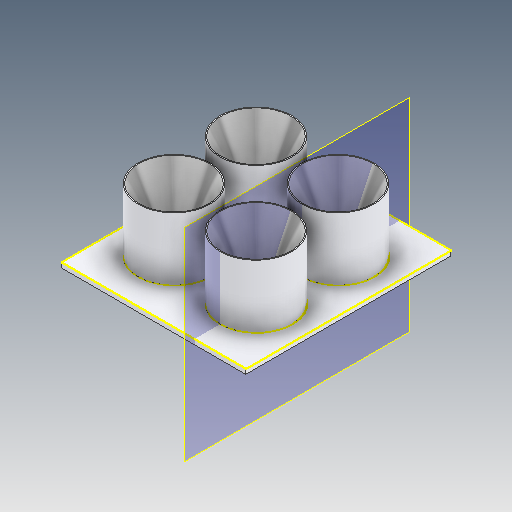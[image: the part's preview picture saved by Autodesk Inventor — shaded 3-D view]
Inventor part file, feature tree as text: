
AUTODESK INVENTOR PART (.ipt)
format: ipt  version: 2020.3 (Build 243373010, 373A)  size: 189,952 bytes
history: native  units: mm
features: other x3, sketch x2, plane x1
ambient origin geometry x8: Origin, YZ Plane, XZ Plane, XY Plane, X Axis, Y Axis, Z Axis, Center Point
bodies: Solid1 (feature_tree)
feature tree (6):
  other  "BottomPart.ipt"
  other  "Solid1::BottomPart.ipt"
  other  "TaggingFeature1"
  sketch  "Sketch1"  dims[d0=10.0mm]
  sketch  "Sketch2"
  plane  "Work Plane1"
